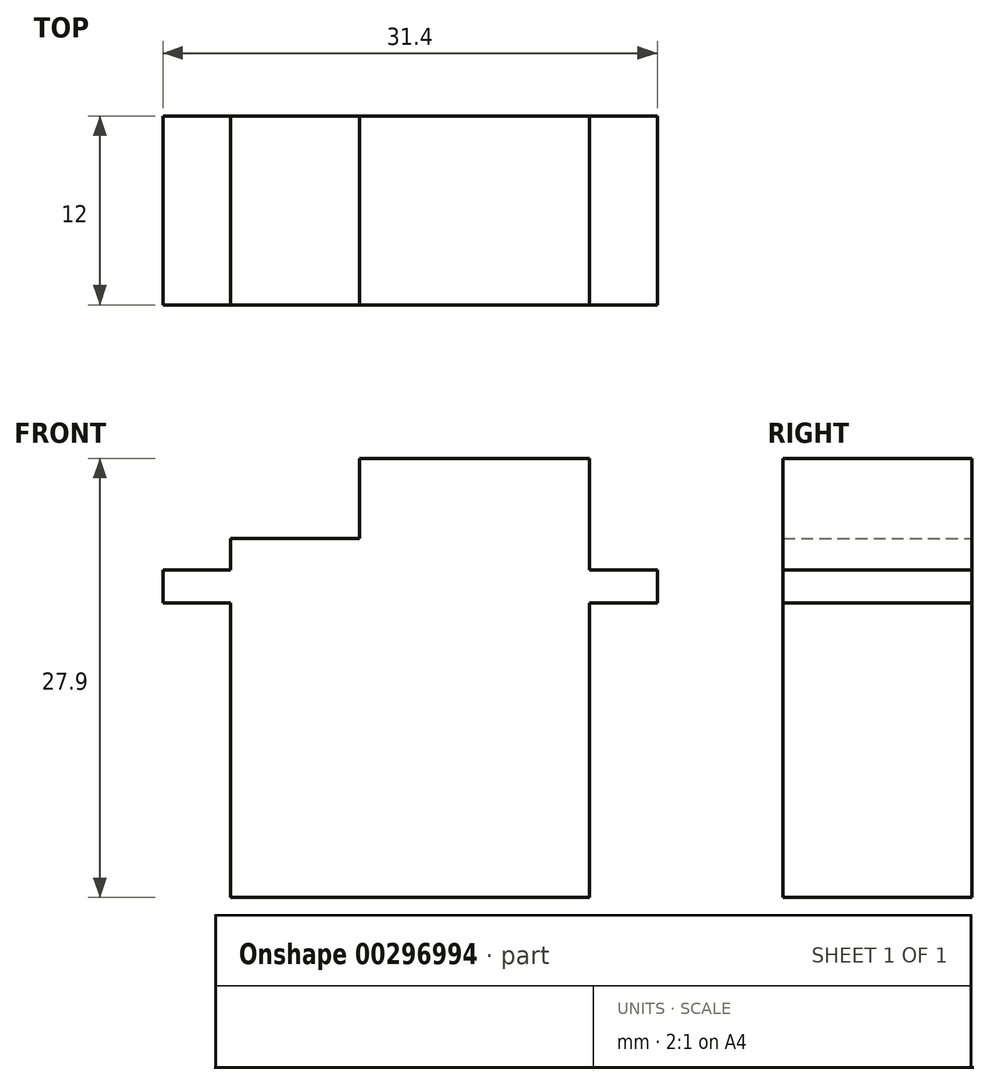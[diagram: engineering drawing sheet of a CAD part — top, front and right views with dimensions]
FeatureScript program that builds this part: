
annotation { "Feature Type Name" : "Feature", "Feature Type Description" : "" }
export const myFeature = defineFeature(function(context is Context, id is Id, definition is map)
    precondition{}
    {
        {
            var Q0;
            Q0=qCreatedBy(makeId("Front.planeOp"),FACE);
            var sketch = newSketch(context, id + "F0", { "sketchPlane" : qUnion([Q0])});
            skLineSegment(sketch, "E0.bottom", {"start": v(0, 4.1) * mm, "end": v(22.8, 4.1) * mm});
            skLineSegment(sketch, "E0.top", {"start": v(0, -18.7) * mm, "end": v(22.8, -18.7) * mm});
            skLineSegment(sketch, "E0.left", {"start": v(0, 4.1) * mm, "end": v(0, -18.7) * mm});
            skLineSegment(sketch, "E0.right", {"start": v(22.8, 4.1) * mm, "end": v(22.8, -18.7) * mm});
            skLineSegment(sketch, "E1.bottom", {"start": v(-4.3, 2.1) * mm, "end": v(27.1, 2.1) * mm});
            skLineSegment(sketch, "E1.top", {"start": v(-4.3, 0) * mm, "end": v(27.1, 0) * mm});
            skLineSegment(sketch, "E1.left", {"start": v(-4.3, 2.1) * mm, "end": v(-4.3, 0) * mm});
            skLineSegment(sketch, "E1.right", {"start": v(27.1, 2.1) * mm, "end": v(27.1, 0) * mm});
            skLineSegment(sketch, "E2.bottom", {"start": v(8.2, 9.2) * mm, "end": v(22.8, 9.2) * mm});
            skLineSegment(sketch, "E2.top", {"start": v(8.2, 4.1) * mm, "end": v(22.8, 4.1) * mm});
            skLineSegment(sketch, "E2.left", {"start": v(8.2, 9.2) * mm, "end": v(8.2, 4.1) * mm});
            skLineSegment(sketch, "E2.right", {"start": v(22.8, 9.2) * mm, "end": v(22.8, 4.1) * mm});
            skLineSegment(sketch, "E3", {"start": v(11.4, -18.7) * mm, "end": v(11.4, 0) * mm, "construction": true});
            skPoint(sketch, "E4", {"position": v(0, 0) * mm});
            skSolve(sketch);
        }
        {
            var Q0;
            {var subQ0=sQuery(id+"F0.wireOp",EDGE,"E0.top");Q0=makeQuery(id+"F0.imprint","IMPRINT",FACE,{"disambiguationData":[TD([[makeQuery(id+"F0.imprint","IMPRINT",EDGE,{"derivedFrom":subQ0}),1.0]])]});}
            var Q1;
            {var subQ5=sQuery(id+"F0.wireOp",EDGE,"E1.left");Q1=makeQuery(id+"F0.imprint","IMPRINT",FACE,{"disambiguationData":[TD([[makeQuery(id+"F0.imprint","IMPRINT",EDGE,{"derivedFrom":subQ5}),1.0]])]});}
            var Q2;
            {var subQ5=sQuery(id+"F0.wireOp",EDGE,"E0.bottom");Q2=makeQuery(id+"F0.imprint","IMPRINT",FACE,{"disambiguationData":[TD([[makeQuery(id+"F0.imprint","IMPRINT",EDGE,{"derivedFrom":subQ5}),-1.0]])]});}
            var Q3;
            {var subQ0=sQuery(id+"F0.wireOp",EDGE,"E1.bottom");var subQ1=sQuery(id+"F0.wireOp",EDGE,"E0.left");var subQ2=makeQuery(id+"F0.imprint","INTERSECT",VERTEX,{"derivedFrom":[subQ1,subQ0]});Q3=makeQuery(id+"F0.imprint","IMPRINT",FACE,{"disambiguationData":[TD([[makeQuery(id+"F0.imprint","IMPRINT",EDGE,{"disambiguationData":[TD([[subQ2,-1.0]])],"derivedFrom":subQ1}),1.0]])]});}
            var Q4;
            Q4=makeQuery(id+"F0.imprint","IMPRINT",FACE,{"disambiguationData":[TD([[makeQuery(id+"F0.imprint","IMPRINT",EDGE,{"derivedFrom":sQuery(id+"F0.wireOp",EDGE,"E2.bottom")}),-1.0]])]});
            var Q5;
            {var subQ5=sQuery(id+"F0.wireOp",EDGE,"E1.right");Q5=makeQuery(id+"F0.imprint","IMPRINT",FACE,{"disambiguationData":[TD([[makeQuery(id+"F0.imprint","IMPRINT",EDGE,{"derivedFrom":subQ5}),-1.0]])]});}
            extrude(context, id + "F1", {"entities" : qUnion([Q0, Q1, Q2, Q3, Q4, Q5]), "depth" : 12 * mm});
        }
    });
